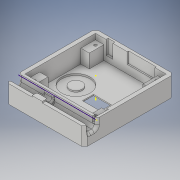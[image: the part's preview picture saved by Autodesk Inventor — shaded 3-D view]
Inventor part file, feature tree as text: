
AUTODESK INVENTOR PART (.ipt)
format: ipt  version: 2019 (Build 230136000, 136)  size: 534,528 bytes
history: native  units: mm
features: move_body x29, sketch x26, extrude x20, direct_edit x11, fillet x4, chamfer x2
ambient origin geometry x8: Origin, YZ Plane, XZ Plane, XY Plane, X Axis, Y Axis, Z Axis, Center Point
bodies: Solid1 (feature_tree)
feature tree (92):
  extrude  "Extrusion1"  Depth=55.0mm
  extrude  "Extrusion2"  Depth=50.0mm
  extrude  "Extrusion3"  Depth=3.0mm TaperAngle=0.0deg
  extrude  "Extrusion4"  Depth=5.5mm
  sketch  "Sketch5"  dims[d10=5.5mm d11=5.5mm]
  sketch  "Sketch6"  dims[d12=5.5mm d13=5.5mm]
  extrude  "Extrusion5"  Depth=5.5mm
  sketch  "Sketch8"  dims[d16=10.0mm d17=0.0mm d18=2.0mm]
  direct_edit  "Direct Edit1"
  extrude  "Extrusion6"  Depth=5.5mm
  direct_edit  "Direct Edit2"
  extrude  "Extrusion7"  Depth=5.5mm
  extrude  "Extrusion8"  Depth=2.0mm
  extrude  "Extrusion9"  Depth=2.0mm
  direct_edit  "Direct Edit3"
  extrude  "Extrusion10"  Depth=25.0mm
  extrude  "Extrusion11"  Depth=1.0mm TaperAngle=0.0deg
  extrude  "Extrusion12"  TaperAngle=0.0deg  [1 undecoded]
  direct_edit  "Direct Edit4"
  extrude  "Extrusion13"  TaperAngle=0.0deg  [1 undecoded]
  direct_edit  "Direct Edit5"
  direct_edit  "Direct Edit6"
  sketch  "Sketch16"  dims[d52=1.0mm d53=0.0mm d54=0.0mm d55=0.0mm d56=-0.1mm]
  extrude  "Extrusion14"  TaperAngle=0.0deg  [1 undecoded]
  direct_edit  "Direct Edit7"
  direct_edit  "Direct Edit8"
  direct_edit  "Direct Edit9"
  sketch  "Sketch18"  dims[d61=1.25mm d62=0.0mm d63=9.2mm d64=1.0mm d65=0.0mm]
  direct_edit  "Direct Edit10"
  extrude  "Extrusion15"  TaperAngle=0.0deg  [1 undecoded]
  extrude  "Extrusion16"  TaperAngle=0.0deg  [1 undecoded]
  direct_edit  "Direct Edit11"
  sketch  "Sketch21"  dims[d76=8.0mm d77=0.0mm d78=3.0mm]
  extrude  "Extrusion17"  Depth=20.5mm
  extrude  "Extrusion18"  Depth=9.2mm
  chamfer  "Chamfer1"  Distance=1.0mm
  chamfer  "Chamfer2"  Distance=2.0mm
  fillet  "Fillet1"  Radius=3.0mm
  fillet  "Fillet2"  Radius=1.0mm
  fillet  "Fillet3"  Radius=3.0mm
  extrude  "Extrusion19"  Depth=3.0mm
  sketch  "Sketch25"  dims[d90=0.0mm d91=0.0mm d92=4.5mm]
  extrude  "Extrusion20"  TaperAngle=0.0deg  [1 undecoded]
  fillet  "Fillet4"  Radius=2.0mm
  sketch  "Sketch1"  dims[d0=55.0mm d1=55.0mm]
  sketch  "Sketch2"  dims[d2=15.0mm d3=0.0mm d4=50.0mm]
  sketch  "Sketch3"  dims[d5=50.0mm d6=3.0mm d7=0.0mm]
  sketch  "Sketch4"  dims[d8=5.5mm d9=5.5mm]
  sketch  "Sketch7"  dims[d14=5.5mm d15=5.5mm]
  sketch  "Sketch9"  dims[d19=2.0mm d20=2.0mm]
  sketch  "Sketch10"  dims[d22=6.0mm d23=0.0mm d24=25.0mm]
  sketch  "Sketch11"  dims[d25=25.0mm d26=1.0mm d27=0.0mm]
  sketch  "Sketch12"  dims[d28=0.0mm d29=0.0mm d30=-0.15mm d31=0.0mm d32=0.0mm d33=-0.15mm]
  sketch  "Sketch13"  dims[d34=0.0mm d35=0.0mm d36=-0.15mm d37=0.0mm d38=0.0mm d39=-0.15mm]
  sketch  "Sketch14"  dims[d40=0.0mm d41=0.0mm d42=-0.15mm d43=0.0mm d44=0.0mm d45=-0.15mm]
  sketch  "Sketch15"  dims[d46=0.0mm d47=0.0mm d48=-0.15mm d49=0.0mm d50=0.0mm d51=-0.15mm]
  sketch  "Sketch17"  dims[d57=0.0mm d58=0.0mm d59=-0.1mm d60=20.5mm]
  sketch  "Sketch19"  dims[d66=2.0mm d67=2.0mm d68=0.0mm]
  sketch  "Sketch20"  dims[d69=0.0mm d70=0.0mm d71=1.0mm d72=3.0mm d73=1.0mm d74=0.0mm d75=3.0mm]
  sketch  "Sketch22"  dims[d79=4.0mm d80=0.0mm d81=0.0mm d82=0.0mm d83=-0.5mm d84=2.0mm]
  sketch  "Sketch23"  dims[d85=4.0mm d86=0.0mm]
  sketch  "Sketch24"  dims[d87=0.0mm d88=0.0mm d89=3.0mm]
  sketch  "Sketch26"  dims[d93=0.0mm d94=0.0mm d95=4.5mm d96=5.0mm d97=2.0mm d98=10.0mm d99=0.0mm d100=0.0mm d101=0.0mm d102=1.0mm d103=0.0mm d104=0.0mm d105=1.0mm d106=0.0mm d107=0.0mm d108=1.0mm d109=0.0mm d110=0.0mm d111=-0.5mm d112=0.0mm d113=0.0mm d114=-0.5mm d115=0.0mm d116=0.0mm d117=-0.5mm d118=0.0mm d119=0.0mm d120=-0.5mm d121=0.0mm d122=0.0mm d123=-0.5mm d124=0.0mm d125=0.0mm d126=-0.5mm d127=0.0mm d128=0.0mm d129=-1.5mm d130=0.0mm d131=0.0mm d132=-1.5mm d133=0.0mm d134=0.0mm d135=-0.75mm d136=0.0mm d137=0.0mm d138=-0.75mm d139=8.0mm d140=0.0mm d141=6.7mm d142=6.7mm d143=5.5mm d144=0.0mm d145=0.0mm d146=0.0mm d147=1.0mm d148=2.5mm d149=0.0mm d150=20.0mm d151=1.0mm d152=8.0mm d153=0.0mm d154=2.0mm d155=2.0mm d156=45.0deg d157=2.0mm d158=2.0mm d159=45.0deg d160=2.0mm d161=2.0mm d162=1.2mm d163=1.6mm d164=4.0mm d165=0.0mm d166=2.5mm d167=0.0mm d168=2.0mm]
  move_body  "Move1"
  move_body  "Move2"
  move_body  "Move3"
  move_body  "Move4"
  move_body  "Move5"
  move_body  "Move6"
  move_body  "Move7"
  move_body  "Move8"
  move_body  "Move9"
  move_body  "Move10"
  move_body  "Move11"
  move_body  "Move12"
  move_body  "Move13"
  move_body  "Move14"
  move_body  "Move15"
  move_body  "Move16"
  move_body  "Move17"
  move_body  "Move18"
  move_body  "Move19"
  move_body  "Move20"
  move_body  "Move21"
  move_body  "Move22"
  move_body  "Move23"
  move_body  "Move24"
  move_body  "Move25"
  move_body  "Move26"
  move_body  "Move27"
  move_body  "Move28"
  move_body  "Move29"
note: 6 required parameter values undecoded (feature->parameter linkage not recoverable at this tier; creation-order binding heuristic only, values carry confidence <= 0.55)
